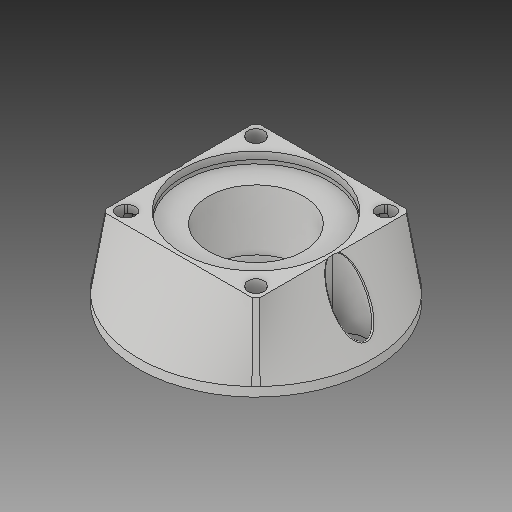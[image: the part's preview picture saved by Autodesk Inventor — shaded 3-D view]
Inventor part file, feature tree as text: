
AUTODESK INVENTOR PART (.ipt)
format: ipt  version: 2019 (Build 230136000, 136)  size: 702,464 bytes
history: native  units: in
note: dims shown in document units (in); Inventor stores cm internally (conversion verified against a paired STEP export)
features: fillet x1
ambient origin geometry x8: Origin, YZ Plane, XZ Plane, XY Plane, X Axis, Y Axis, Z Axis, Center Point
bodies: Solid1 (feature_tree)
feature tree (1):
  fillet  "Fillet3"  [1 undecoded]
note: 1 required parameter value undecoded (feature->parameter linkage not recoverable at this tier; creation-order binding heuristic only, values carry confidence <= 0.55)
